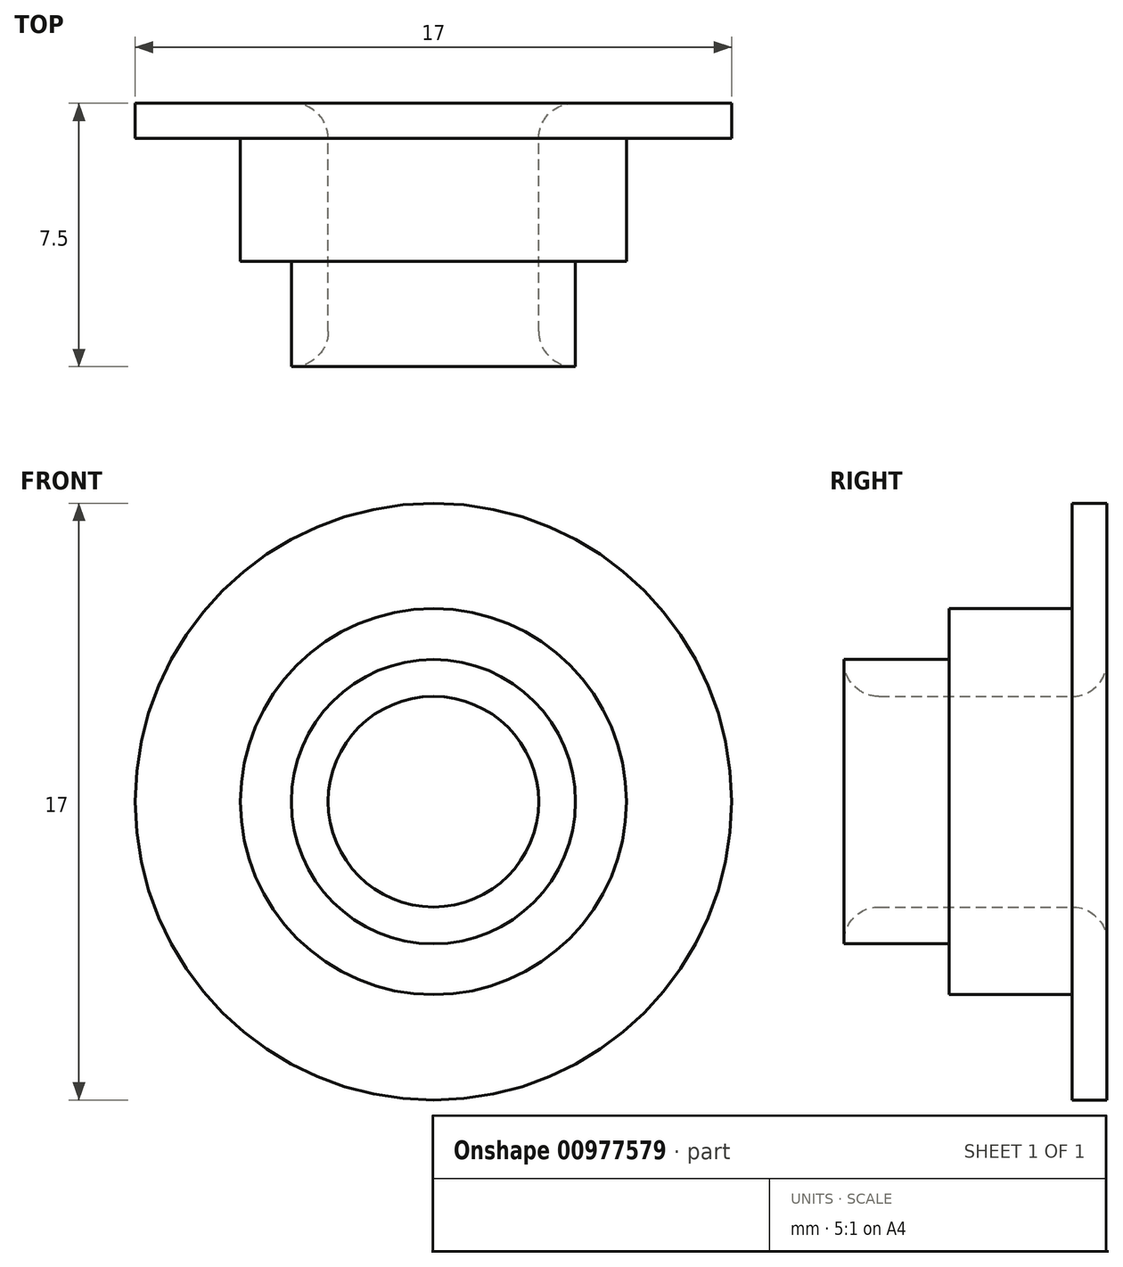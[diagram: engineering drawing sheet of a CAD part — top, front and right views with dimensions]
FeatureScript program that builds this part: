
annotation { "Feature Type Name" : "Feature", "Feature Type Description" : "" }
export const myFeature = defineFeature(function(context is Context, id is Id, definition is map)
    precondition{}
    {
        {
            var Q0;
            Q0=qCreatedBy(makeId("Front.planeOp"),FACE);
            var sketch = newSketch(context, id + "F0", { "sketchPlane" : qUnion([Q0])});
            skCircle(sketch, "E0", {"center": v(0, 0) * mm, "radius": 5.5 * mm});
            skCircle(sketch, "E1.0", {"center": v(0, 0) * mm, "radius": 8.5 * mm});
            skCircle(sketch, "E2", {"center": v(0, 0) * mm, "radius": 3 * mm});
            skCircle(sketch, "E3", {"center": v(0, 0) * mm, "radius": 4.05 * mm});
            skSolve(sketch);
        }
        {
            var Q0;
            Q0=makeQuery(id+"F0.imprint","IMPRINT",FACE,{"disambiguationData":[TD([[makeQuery(id+"F0.imprint","IMPRINT",EDGE,{"derivedFrom":sQuery(id+"F0.wireOp",EDGE,"E0")}),-1.0]])]});
            extrude(context, id + "F1", {"entities" : qUnion([Q0]), "depth" : 1 * mm, "offsetDistance" : 25 * mm});
        }
        {
            var Q0;
            Q0=makeQuery(id+"F0.imprint","IMPRINT",FACE,{"disambiguationData":[TD([[makeQuery(id+"F0.imprint","IMPRINT",EDGE,{"derivedFrom":sQuery(id+"F0.wireOp",EDGE,"E0")}),1.0]])]});
            extrude(context, id + "F2", {"entities" : qUnion([Q0]), "operationType" : NewBodyOperationType.ADD, "depth" : 4.5 * mm, "offsetDistance" : 25 * mm});
        }
        {
            var Q0;
            Q0=makeQuery(id+"F0.imprint","IMPRINT",FACE,{"disambiguationData":[TD([[makeQuery(id+"F0.imprint","IMPRINT",EDGE,{"derivedFrom":sQuery(id+"F0.wireOp",EDGE,"E2")}),-1.0]])]});
            extrude(context, id + "F3", {"entities" : qUnion([Q0]), "operationType" : NewBodyOperationType.ADD, "depth" : 7.5 * mm, "offsetDistance" : 25 * mm});
        }
        {
            var Q0;
            Q0=makeQuery(id+"F3.opExtrude","CAP_EDGE",EDGE,{"disambiguationData":[OSD([sQuery(id+"F0.wireOp",EDGE,"E2")])],"isStart":false});
            fillet(context, id + "F4", {"entities" : qUnion([Q0]), "radius" : 1 * mm, "tangentPropagation" : true, "allowEdgeOverflow" : false});
        }
        {
            var Q0;
            Q0=makeQuery(id+"F3.opExtrude","CAP_EDGE",EDGE,{"disambiguationData":[OSD([sQuery(id+"F0.wireOp",EDGE,"E2")])],"isStart":true});
            fillet(context, id + "F5", {"entities" : qUnion([Q0]), "radius" : 1 * mm, "tangentPropagation" : true, "allowEdgeOverflow" : false});
        }
    });
